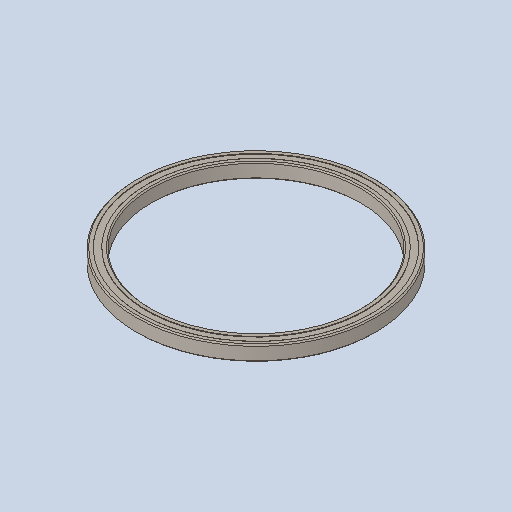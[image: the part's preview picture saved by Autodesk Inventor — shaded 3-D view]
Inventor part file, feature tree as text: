
AUTODESK INVENTOR PART (.ipt)
format: ipt  version: 2023.4 (Build 274418000, 418)  size: 128,000 bytes
history: native  units: in
note: dims shown in document units (in); Inventor stores cm internally (conversion verified against a paired STEP export)
features: revolve x1
ambient origin geometry x8: Origin, YZ Plane, XZ Plane, XY Plane, X Axis, Y Axis, Z Axis, Center Point
bodies: Solid1 (feature_tree)
feature tree (1):
  revolve  "Revolve1"  [1 undecoded]
note: 1 required parameter value undecoded (feature->parameter linkage not recoverable at this tier; creation-order binding heuristic only, values carry confidence <= 0.55)
